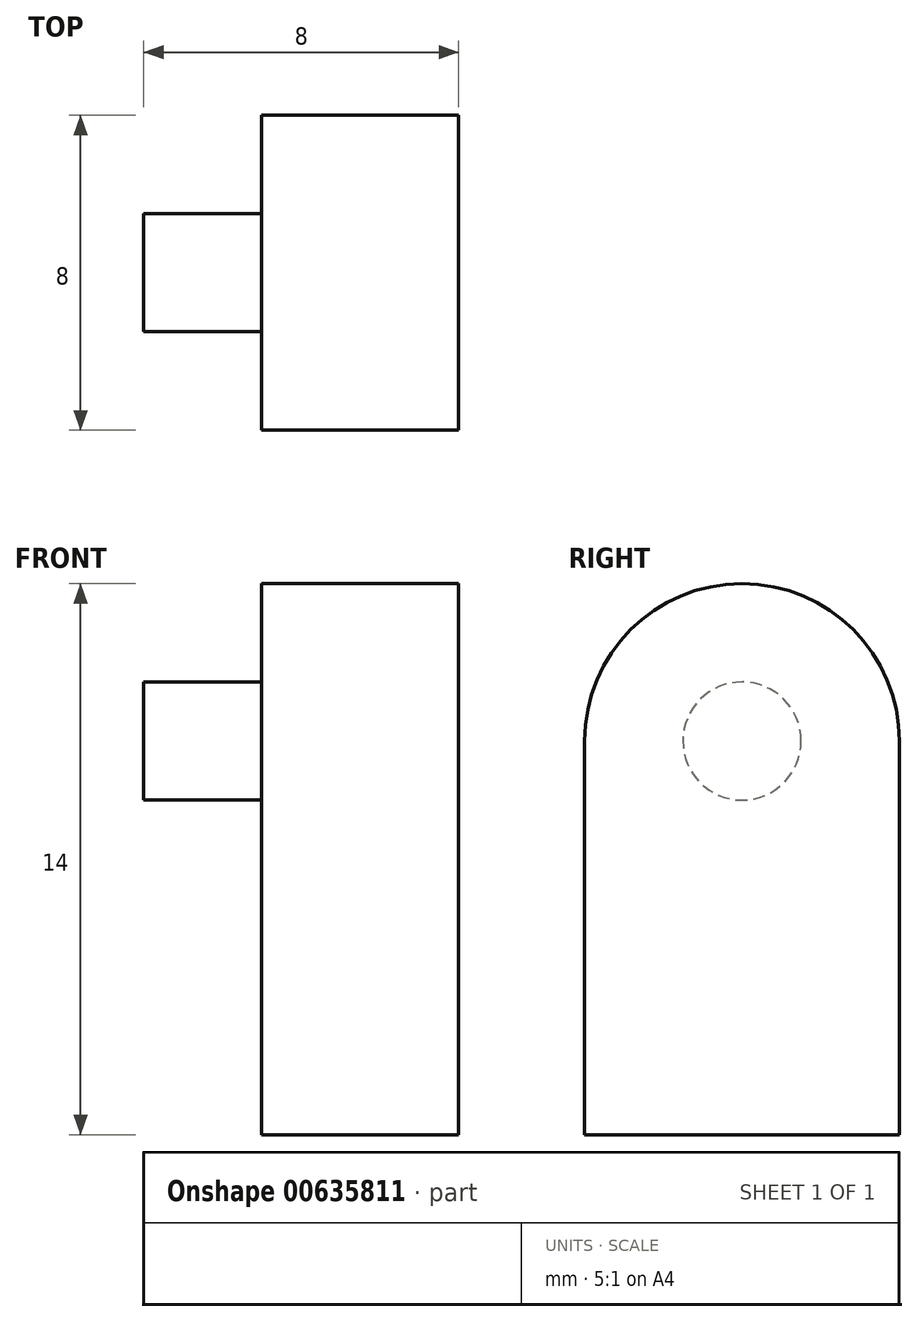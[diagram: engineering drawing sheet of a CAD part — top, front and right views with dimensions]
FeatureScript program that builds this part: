
annotation { "Feature Type Name" : "Feature", "Feature Type Description" : "" }
export const myFeature = defineFeature(function(context is Context, id is Id, definition is map)
    precondition{}
    {
        {
            var Q0;
            Q0=qCreatedBy(makeId("Right.planeOp"),FACE);
            var sketch = newSketch(context, id + "F0", { "sketchPlane" : qUnion([Q0])});
            skCircle(sketch, "E0", {"center": v(0, 0) * mm, "radius": 1.5 * mm});
            skSolve(sketch);
        }
        {
            var Q0;
            Q0 = qSketchRegion(id + "F0", true);
            extrude(context, id + "F1", {"entities" : qUnion([Q0]), "depth" : 3 * mm, "offsetDistance" : 25.4 * mm});
        }
        {
            var Q0;
            Q0=makeQuery(id+"F1.opExtrude","CAP_FACE",FACE,{"disambiguationData":[OSD([sQuery(id+"F0.wireOp",EDGE,"E0")])],"isStart":false});
            var sketch = newSketch(context, id + "F2", { "sketchPlane" : qUnion([Q0])});
            skArc(sketch, "E1", {"start": v(4, 0) * mm, "mid": v(0, 4) * mm, "end": v(-4, 0) * mm});
            skLineSegment(sketch, "E2.top", {"start": v(-4, -10) * mm, "end": v(4, -10) * mm});
            skLineSegment(sketch, "E2.left", {"start": v(-4, 0) * mm, "end": v(-4, -10) * mm});
            skLineSegment(sketch, "E2.right", {"start": v(4, 0) * mm, "end": v(4, -10) * mm});
            skPoint(sketch, "E2.middle", {"position": v(0, -5) * mm});
            skLineSegment(sketch, "E3", {"start": v(4, -10) * mm, "end": v(-3.1, -16.3) * mm, "construction": true});
            skLineSegment(sketch, "E4", {"start": v(-3.1, -16.3) * mm, "end": v(-6.62, -12.32) * mm, "construction": true});
            skLineSegment(sketch, "E5", {"start": v(-6.62, -12.32) * mm, "end": v(-4, -10) * mm, "construction": true});
            skLineSegment(sketch, "E6", {"start": v(-4.86, -14.3) * mm, "end": v(-2.9, -12.53) * mm, "construction": true});
            skSolve(sketch);
        }
        {
            var Q0;
            Q0 = qSketchRegion(id + "F2", true);
            extrude(context, id + "F3", {"entities" : qUnion([Q0]), "operationType" : NewBodyOperationType.ADD, "depth" : 5 * mm, "offsetDistance" : 25.4 * mm});
        }
    });
